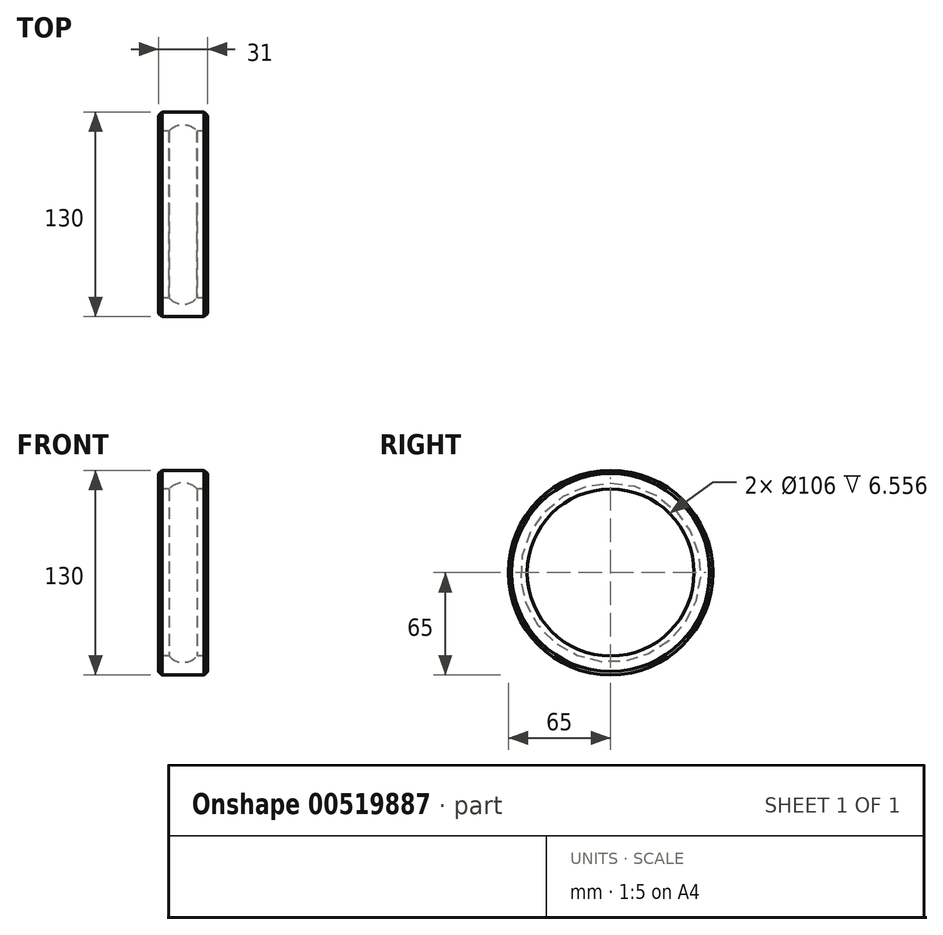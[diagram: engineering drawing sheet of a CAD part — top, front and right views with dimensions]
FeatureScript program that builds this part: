
annotation { "Feature Type Name" : "Feature", "Feature Type Description" : "" }
export const myFeature = defineFeature(function(context is Context, id is Id, definition is map)
    precondition{}
    {
        {
            var Q0;
            Q0=qCreatedBy(makeId("Top.planeOp"),FACE);
            var sketch = newSketch(context, id + "F0", { "sketchPlane" : qUnion([Q0])});
            skLineSegment(sketch, "E0.bottom", {"start": v(-15.5, 65) * mm, "end": v(15.5, 65) * mm});
            skLineSegment(sketch, "E0.top", {"start": v(-15.5, 53) * mm, "end": v(-8.94, 53) * mm});
            skLineSegment(sketch, "E0.left", {"start": v(-15.5, 65) * mm, "end": v(-15.5, 53) * mm});
            skLineSegment(sketch, "E0.right", {"start": v(15.5, 65) * mm, "end": v(15.5, 53) * mm});
            skPoint(sketch, "E0.middle", {"position": v(0, 59) * mm});
            skLineSegment(sketch, "E1", {"start": v(0, 0) * mm, "end": v(0, 53) * mm, "construction": true});
            skLineSegment(sketch, "E2.trimOffspring", {"start": v(8.94, 53) * mm, "end": v(15.5, 53) * mm});
            skLineSegment(sketch, "E3", {"start": v(-75.82, 0) * mm, "end": v(76.85, 0) * mm, "construction": true});
            skArc(sketch, "E4", {"start": v(-8.94, 53) * mm, "mid": v(0, 57) * mm, "end": v(8.94, 53) * mm});
            skPoint(sketch, "E5.orphan", {"position": v(-2.39, 53) * mm});
            skSolve(sketch);
        }
        {
            var Q0;
            Q0=makeQuery(id+"F0.imprint","IMPRINT",FACE,{"disambiguationData":[TD([[makeQuery(id+"F0.imprint","IMPRINT",EDGE,{"derivedFrom":sQuery(id+"F0.wireOp",EDGE,"E0.bottom")}),-1.0]])]});
            var Q1;
            Q1=sQuery(id+"F0.wireOp",EDGE,"E3");
            revolve(context, id + "F1", {"entities" : qUnion([Q0]), "axis" : qUnion([Q1]), "revolveType" : RevolveType.FULL});
        }
        {
            var Q0;
            Q0=makeQuery(id+"F1.opRevolve","SWEPT_FACE",FACE,{"disambiguationData":[OSD([sQuery(id+"F0.wireOp",EDGE,"E0.bottom")])]});
            chamfer(context, id + "F2", {"entities" : qUnion([Q0]), "width" : 2.1 * mm, "tangentPropagation" : true});
        }
    });
